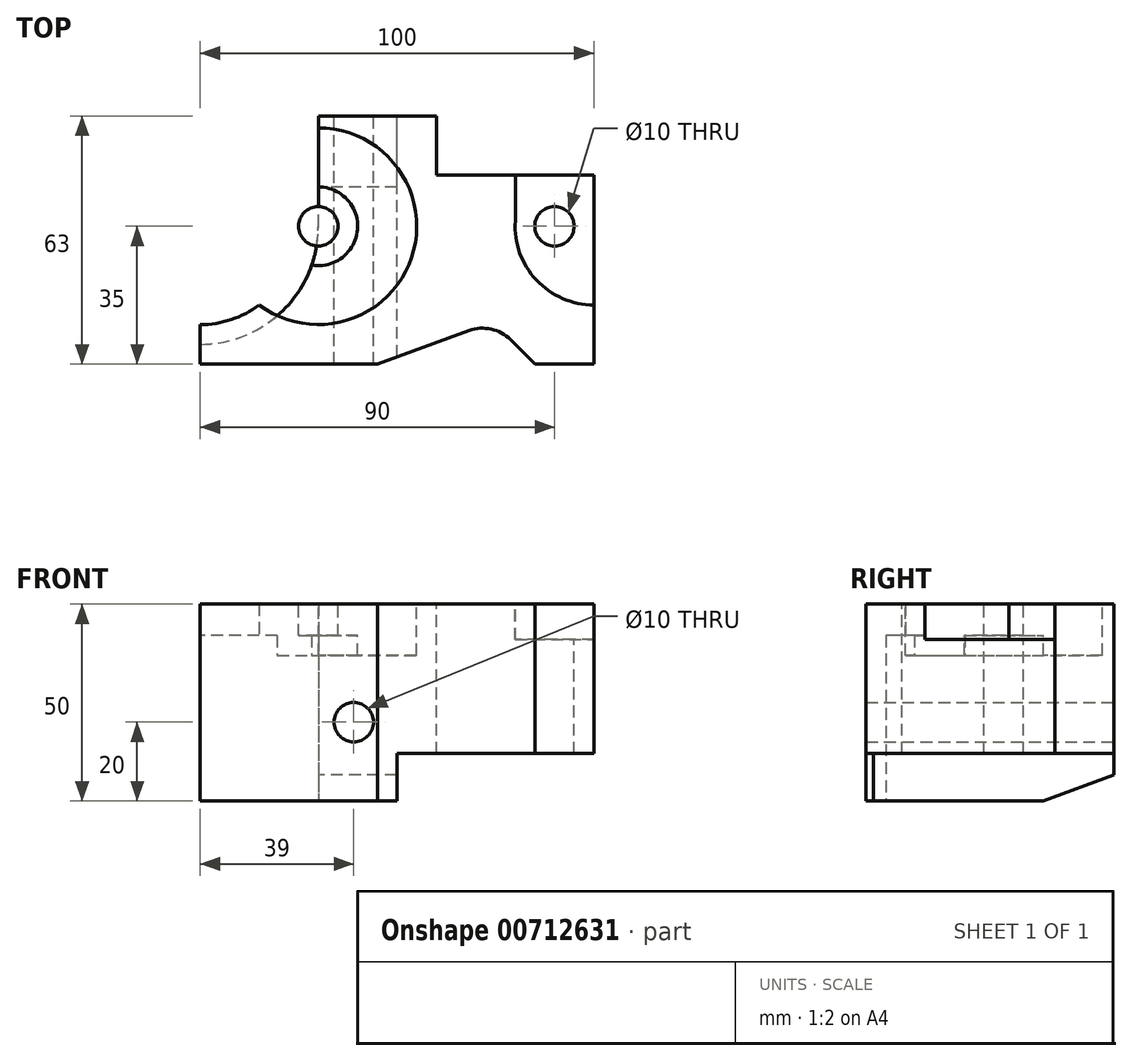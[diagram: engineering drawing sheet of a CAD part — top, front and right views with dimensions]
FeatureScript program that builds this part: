
annotation { "Feature Type Name" : "Feature", "Feature Type Description" : "" }
export const myFeature = defineFeature(function(context is Context, id is Id, definition is map)
    precondition{}
    {
        {
            var Q0;
            Q0=qCreatedBy(makeId("Top.planeOp"),FACE);
            var sketch = newSketch(context, id + "F0", { "sketchPlane" : qUnion([Q0])});
            skLineSegment(sketch, "E0.bottom", {"start": v(0, 0) * mm, "end": v(-100, 0) * mm});
            skLineSegment(sketch, "E0.top", {"start": v(0, 63) * mm, "end": v(-100, 63) * mm});
            skLineSegment(sketch, "E0.left", {"start": v(0, 0) * mm, "end": v(0, 63) * mm});
            skLineSegment(sketch, "E0.right", {"start": v(-100, 0) * mm, "end": v(-100, 63) * mm});
            skSolve(sketch);
        }
        {
            var Q0;
            Q0=makeQuery(id+"F0.imprint","IMPRINT",FACE,{"disambiguationData":[TD([[makeQuery(id+"F0.imprint","IMPRINT",EDGE,{"derivedFrom":sQuery(id+"F0.wireOp",EDGE,"E0.bottom")}),-1.0]])]});
            extrude(context, id + "F1", {"entities" : qUnion([Q0]), "depth" : 50 * mm, "offsetDistance" : 25 * mm});
        }
        {
            var Q0;
            Q0=makeQuery(id+"F1.opExtrude","CAP_FACE",FACE,{"disambiguationData":[OSD([sQuery(id+"F0.wireOp",EDGE,"E0.bottom"),sQuery(id+"F0.wireOp",EDGE,"E0.top"),sQuery(id+"F0.wireOp",EDGE,"E0.left"),sQuery(id+"F0.wireOp",EDGE,"E0.right")])],"isStart":false});
            var sketch = newSketch(context, id + "F2", { "sketchPlane" : qUnion([Q0])});
            skLineSegment(sketch, "E1.bottom", {"start": v(0, 63) * mm, "end": v(-40, 63) * mm});
            skLineSegment(sketch, "E1.top", {"start": v(0, 48) * mm, "end": v(-40, 48) * mm});
            skLineSegment(sketch, "E1.left", {"start": v(0, 63) * mm, "end": v(0, 48) * mm});
            skLineSegment(sketch, "E1.right", {"start": v(-40, 63) * mm, "end": v(-40, 48) * mm});
            skSolve(sketch);
        }
        {
            var Q0;
            Q0=makeQuery(id+"F2.imprint","IMPRINT",FACE,{"disambiguationData":[TD([[makeQuery(id+"F2.imprint","IMPRINT",EDGE,{"derivedFrom":sQuery(id+"F2.wireOp",EDGE,"E1.bottom")}),1.0]])]});
            extrude(context, id + "F3", {"entities" : qUnion([Q0]), "operationType" : NewBodyOperationType.REMOVE, "endBound" : BoundingType.THROUGH_ALL, "oppositeDirection" : true, "depth" : 25 * mm, "offsetDistance" : 25 * mm});
        }
        {
            var Q0;
            Q0=makeQuery(id+"F1.opExtrude","CAP_FACE",FACE,{"disambiguationData":[OSD([sQuery(id+"F0.wireOp",EDGE,"E0.bottom"),sQuery(id+"F0.wireOp",EDGE,"E0.top"),sQuery(id+"F0.wireOp",EDGE,"E0.left"),sQuery(id+"F0.wireOp",EDGE,"E0.right")])],"isStart":false});
            var sketch = newSketch(context, id + "F4", { "sketchPlane" : qUnion([Q0])});
            skArc(sketch, "E2", {"start": v(-19.96, 36.28) * mm, "mid": v(-14.59, 21.32) * mm, "end": v(0, 15) * mm});
            skLineSegment(sketch, "E3", {"start": v(-19.96, 33.72) * mm, "end": v(-19.96, 48) * mm});
            skLineSegment(sketch, "E4", {"start": v(-19.96, 48) * mm, "end": v(0, 48) * mm});
            skLineSegment(sketch, "E5", {"start": v(0, 48) * mm, "end": v(0, 15) * mm});
            skSolve(sketch);
        }
        {
            var Q0;
            Q0 = qSketchRegion(id + "F4", true);
            extrude(context, id + "F5", {"entities" : qUnion([Q0]), "operationType" : NewBodyOperationType.REMOVE, "oppositeDirection" : true, "depth" : 9 * mm, "offsetDistance" : 25 * mm});
        }
        {
            var Q0;
            Q0=makeQuery(id+"F5.boolean.opBoolean","COPY",FACE,{"derivedFrom":makeQuery(id+"F5.opExtrude","CAP_FACE",FACE,{"disambiguationData":[OSD([sQuery(id+"F4.wireOp",EDGE,"E2"),sQuery(id+"F4.wireOp",EDGE,"E3"),sQuery(id+"F4.wireOp",EDGE,"E4"),sQuery(id+"F4.wireOp",EDGE,"E5")])],"isStart":false})});
            var sketch = newSketch(context, id + "F6", { "sketchPlane" : qUnion([Q0])});
            skCircle(sketch, "E6", {"center": v(-10, 35) * mm, "radius": 5 * mm});
            skSolve(sketch);
        }
        {
            var Q0;
            Q0 = qSketchRegion(id + "F6", true);
            extrude(context, id + "F7", {"entities" : qUnion([Q0]), "operationType" : NewBodyOperationType.REMOVE, "endBound" : BoundingType.THROUGH_ALL, "oppositeDirection" : true, "depth" : 25 * mm, "offsetDistance" : 25 * mm});
        }
        {
            var Q0;
            Q0=makeQuery(id+"F1.opExtrude","SWEPT_FACE",FACE,{"disambiguationData":[OSD([sQuery(id+"F0.wireOp",EDGE,"E0.top")])]});
            var sketch = newSketch(context, id + "F8", { "sketchPlane" : qUnion([Q0])});
            skLineSegment(sketch, "E7.bottom", {"start": v(50, 0) * mm, "end": v(0, 0) * mm});
            skLineSegment(sketch, "E7.top", {"start": v(50, 12) * mm, "end": v(0, 12) * mm});
            skLineSegment(sketch, "E7.left", {"start": v(50, 0) * mm, "end": v(50, 12) * mm});
            skLineSegment(sketch, "E7.right", {"start": v(0, 0) * mm, "end": v(0, 12) * mm});
            skSolve(sketch);
        }
        {
            var Q0;
            Q0 = qSketchRegion(id + "F8", true);
            extrude(context, id + "F9", {"entities" : qUnion([Q0]), "operationType" : NewBodyOperationType.REMOVE, "endBound" : BoundingType.THROUGH_ALL, "oppositeDirection" : true, "depth" : 25 * mm, "offsetDistance" : 25 * mm});
        }
        {
            var Q0;
            Q0=makeQuery(id+"F1.opExtrude","CAP_FACE",FACE,{"disambiguationData":[OSD([sQuery(id+"F0.wireOp",EDGE,"E0.bottom"),sQuery(id+"F0.wireOp",EDGE,"E0.top"),sQuery(id+"F0.wireOp",EDGE,"E0.left"),sQuery(id+"F0.wireOp",EDGE,"E0.right")])],"isStart":false});
            var sketch = newSketch(context, id + "F10", { "sketchPlane" : qUnion([Q0])});
            skLineSegment(sketch, "E8", {"start": v(-15, 0) * mm, "end": v(-21.17, 6.17) * mm});
            skLineSegment(sketch, "E9", {"start": v(-31.66, 8.5) * mm, "end": v(-55, 0) * mm});
            skPoint(sketch, "E10.visualSharp", {"position": v(-25.67, 10.67) * mm});
            skArc(sketch, "E10.filletArc", {"start": v(-21.17, 6.17) * mm, "mid": v(-26.08, 8.86) * mm, "end": v(-31.66, 8.5) * mm});
            skLineSegment(sketch, "E11", {"start": v(-55, 0) * mm, "end": v(-15, 0) * mm});
            skSolve(sketch);
        }
        {
            var Q0;
            Q0 = qSketchRegion(id + "F10", true);
            extrude(context, id + "F11", {"entities" : qUnion([Q0]), "operationType" : NewBodyOperationType.REMOVE, "endBound" : BoundingType.THROUGH_ALL, "oppositeDirection" : true, "depth" : 25 * mm, "offsetDistance" : 25 * mm});
        }
        {
            var Q0;
            Q0=makeQuery(id+"F1.opExtrude","CAP_FACE",FACE,{"disambiguationData":[OSD([sQuery(id+"F0.wireOp",EDGE,"E0.bottom"),sQuery(id+"F0.wireOp",EDGE,"E0.top"),sQuery(id+"F0.wireOp",EDGE,"E0.left"),sQuery(id+"F0.wireOp",EDGE,"E0.right")])],"isStart":false});
            var sketch = newSketch(context, id + "F12", { "sketchPlane" : qUnion([Q0])});
            skCircle(sketch, "E12", {"center": v(-70, 35) * mm, "radius": 5 * mm});
            skCircle(sketch, "E13", {"center": v(-70, 35) * mm, "radius": 10 * mm});
            skCircle(sketch, "E14", {"center": v(-70, 35) * mm, "radius": 25 * mm});
            skSolve(sketch);
        }
        {
            var Q0;
            Q0=makeQuery(id+"F12.imprint","IMPRINT",FACE,{"disambiguationData":[TD([[makeQuery(id+"F12.imprint","IMPRINT",EDGE,{"derivedFrom":sQuery(id+"F12.wireOp",EDGE,"E12")}),-1.0]])]});
            extrude(context, id + "F13", {"entities" : qUnion([Q0]), "operationType" : NewBodyOperationType.REMOVE, "oppositeDirection" : true, "depth" : 8 * mm, "offsetDistance" : 25 * mm});
        }
        {
            var Q0;
            Q0 = qSketchRegion(id + "F12", true);
            extrude(context, id + "F14", {"entities" : qUnion([Q0]), "operationType" : NewBodyOperationType.ADD, "oppositeDirection" : true, "depth" : 13 * mm, "offsetDistance" : 25 * mm});
        }
        {
            var Q0;
            {var subQ0=sQuery(id+"F0.wireOp",EDGE,"E0.right");var subQ1=sQuery(id+"F0.wireOp",EDGE,"E0.top");var subQ2=sQuery(id+"F0.wireOp",EDGE,"E0.bottom");var subQ3=sQuery(id+"F0.wireOp",EDGE,"E0.left");Q0=makeQuery(id+"F13.boolean.opBoolean","SPLIT",FACE,{"disambiguationData":[TD([makeQuery(id+"F1.opExtrude","SWEPT_FACE",FACE,{"disambiguationData":[OSD([subQ2])]})])],"derivedFrom":makeQuery(id+"F1.opExtrude","CAP_FACE",FACE,{"disambiguationData":[OSD([subQ2,subQ1,subQ3,subQ0])],"isStart":false})});}
            var sketch = newSketch(context, id + "F15", { "sketchPlane" : qUnion([Q0])});
            skCircle(sketch, "E15", {"center": v(-70, 35) * mm, "radius": 25 * mm});
            skSolve(sketch);
        }
        {
            var Q0;
            Q0=makeQuery(id+"F15.imprint","IMPRINT",FACE,{"disambiguationData":[TD([[makeQuery(id+"F15.imprint","IMPRINT",EDGE,{"derivedFrom":sQuery(id+"F15.wireOp",EDGE,"E15")}),1.0]])]});
            extrude(context, id + "F16", {"entities" : qUnion([Q0]), "operationType" : NewBodyOperationType.REMOVE, "oppositeDirection" : true, "depth" : 13 * mm, "offsetDistance" : 25 * mm});
        }
        {
            var Q0;
            Q0=makeQuery(id+"F1.opExtrude","SWEPT_FACE",FACE,{"disambiguationData":[OSD([sQuery(id+"F0.wireOp",EDGE,"E0.right")])]});
            var sketch = newSketch(context, id + "F17", { "sketchPlane" : qUnion([Q0])});
            skLineSegment(sketch, "E16", {"start": v(-63, 0) * mm, "end": v(-45, 0) * mm});
            skLineSegment(sketch, "E17", {"start": v(-45, 0) * mm, "end": v(-63, 6.55) * mm});
            skLineSegment(sketch, "E18", {"start": v(-63, 6.55) * mm, "end": v(-63, 0) * mm});
            skSolve(sketch);
        }
        {
            var Q0;
            Q0=makeQuery(id+"F17.imprint","IMPRINT",FACE,{"disambiguationData":[TD([[makeQuery(id+"F17.imprint","IMPRINT",EDGE,{"derivedFrom":sQuery(id+"F17.wireOp",EDGE,"E16")}),-1.0]])]});
            extrude(context, id + "F18", {"entities" : qUnion([Q0]), "operationType" : NewBodyOperationType.REMOVE, "endBound" : BoundingType.THROUGH_ALL, "oppositeDirection" : true, "depth" : 25 * mm, "offsetDistance" : 25 * mm});
        }
        {
            var Q0;
            Q0=makeQuery(id+"F1.opExtrude","CAP_FACE",FACE,{"disambiguationData":[OSD([sQuery(id+"F0.wireOp",EDGE,"E0.bottom"),sQuery(id+"F0.wireOp",EDGE,"E0.top"),sQuery(id+"F0.wireOp",EDGE,"E0.left"),sQuery(id+"F0.wireOp",EDGE,"E0.right")])],"isStart":true});
            var sketch = newSketch(context, id + "F19", { "sketchPlane" : qUnion([Q0])});
            skCircle(sketch, "E19", {"center": v(-100, -35) * mm, "radius": 25 * mm});
            skCircle(sketch, "E20", {"center": v(-100, -35) * mm, "radius": 30 * mm});
            skLineSegment(sketch, "E21", {"start": v(-70, -35) * mm, "end": v(-70, -63) * mm});
            skLineSegment(sketch, "E22", {"start": v(-70, -63) * mm, "end": v(-99.79, -63) * mm});
            skSolve(sketch);
        }
        {
            var Q0;
            {var subQ0=sQuery(id+"F19.wireOp",EDGE,"E19");var subQ1=sQuery(id+"F0.wireOp",EDGE,"E0.right");var subQ2=makeQuery(id+"F1.opExtrude","CAP_EDGE",EDGE,{"disambiguationData":[OSD([subQ1])],"isStart":true});var subQ3=makeQuery(id+"F19.imprint","INTERSECT",VERTEX,{"derivedFrom":[subQ2,subQ0]});Q0=makeQuery(id+"F19.imprint","IMPRINT",FACE,{"disambiguationData":[TD([[makeQuery(id+"F19.imprint","IMPRINT",EDGE,{"disambiguationData":[TD([[subQ3,1.0]])],"derivedFrom":subQ0}),1.0]])]});}
            var Q1;
            {var subQ0=sQuery(id+"F19.wireOp",EDGE,"E19");var subQ1=sQuery(id+"F0.wireOp",EDGE,"E0.right");var subQ2=makeQuery(id+"F1.opExtrude","CAP_EDGE",EDGE,{"disambiguationData":[OSD([subQ1])],"isStart":true});var subQ3=makeQuery(id+"F19.imprint","INTERSECT",VERTEX,{"derivedFrom":[subQ2,subQ0]});Q1=makeQuery(id+"F19.imprint","IMPRINT",FACE,{"disambiguationData":[TD([[makeQuery(id+"F19.imprint","IMPRINT",EDGE,{"disambiguationData":[TD([[subQ3,-1.0]])],"derivedFrom":subQ0}),1.0]])]});}
            extrude(context, id + "F20", {"entities" : qUnion([Q0, Q1]), "operationType" : NewBodyOperationType.REMOVE, "endBound" : BoundingType.THROUGH_ALL, "oppositeDirection" : true, "depth" : 25 * mm, "offsetDistance" : 25 * mm});
        }
        {
            var Q0;
            Q0 = qSketchRegion(id + "F19", true);
            extrude(context, id + "F21", {"entities" : qUnion([Q0]), "operationType" : NewBodyOperationType.REMOVE, "oppositeDirection" : true, "depth" : 42 * mm, "offsetDistance" : 25 * mm});
        }
        {
            var Q0;
            {var subQ0=sQuery(id+"F19.wireOp",EDGE,"E19");var subQ1=sQuery(id+"F19.wireOp",EDGE,"E21");Q0=makeQuery(id+"F21.boolean.opBoolean","COPY",FACE,{"disambiguationData":[TD([makeQuery(id+"F1.opExtrude","SWEPT_FACE",FACE,{"disambiguationData":[OSD([sQuery(id+"F0.wireOp",EDGE,"E0.top")])]}),makeQuery(id+"F1.opExtrude","SWEPT_FACE",FACE,{"disambiguationData":[OSD([sQuery(id+"F0.wireOp",EDGE,"E0.right")])]}),makeQuery(id+"F16.boolean.opBoolean","COPY",FACE,{"derivedFrom":makeQuery(id+"F16.opExtrude","SWEPT_FACE",FACE,{"disambiguationData":[OSD([sQuery(id+"F15.wireOp",EDGE,"E15")])]})}),makeQuery(id+"F20.boolean.opBoolean","COPY",FACE,{"derivedFrom":makeQuery(id+"F20.opExtrude","SWEPT_FACE",FACE,{"disambiguationData":[OSD([subQ0])]})}),makeQuery(id+"F21.opExtrude","SWEPT_FACE",FACE,{"disambiguationData":[OSD([subQ1])]})])],"derivedFrom":makeQuery(id+"F21.opExtrude","CAP_FACE",FACE,{"disambiguationData":[OSD([subQ0,sQuery(id+"F19.wireOp",EDGE,"E20"),subQ1,sQuery(id+"F19.wireOp",EDGE,"E22")])],"isStart":false})});}
            var sketch = newSketch(context, id + "F22", { "sketchPlane" : qUnion([Q0])});
            skLineSegment(sketch, "E23.bottom", {"start": v(-70, -63) * mm, "end": v(-100.84, -63) * mm});
            skLineSegment(sketch, "E23.top", {"start": v(-70, -50.54) * mm, "end": v(-100.84, -50.54) * mm});
            skLineSegment(sketch, "E23.left", {"start": v(-70, -63) * mm, "end": v(-70, -50.54) * mm});
            skLineSegment(sketch, "E23.right", {"start": v(-100.84, -63) * mm, "end": v(-100.84, -50.54) * mm});
            skSolve(sketch);
        }
        {
            var Q0;
            {var subQ5=sQuery(id+"F22.wireOp",EDGE,"E23.top");Q0=makeQuery(id+"F22.imprint","IMPRINT",FACE,{"disambiguationData":[TD([[makeQuery(id+"F22.imprint","IMPRINT",EDGE,{"derivedFrom":subQ5}),1.0]])]});}
            var Q1;
            {var subQ0=sQuery(id+"F19.wireOp",EDGE,"E19");Q1=makeQuery(id+"F22.imprint","IMPRINT",FACE,{"disambiguationData":[TD([[makeQuery(id+"F22.imprint","IMPRINT",EDGE,{"derivedFrom":makeQuery(id+"F21.boolean.opBoolean","COPY",EDGE,{"disambiguationData":[OD(1.0)],"derivedFrom":makeQuery(id+"F21.opExtrude","CAP_EDGE",EDGE,{"disambiguationData":[OSD([subQ0])],"isStart":false})})}),-1.0]])]});}
            extrude(context, id + "F23", {"entities" : qUnion([Q0, Q1]), "operationType" : NewBodyOperationType.REMOVE, "endBound" : BoundingType.THROUGH_ALL, "oppositeDirection" : true, "depth" : 25 * mm, "offsetDistance" : 25 * mm});
        }
        {
            var Q0;
            Q0=makeQuery(id+"F1.opExtrude","SWEPT_FACE",FACE,{"disambiguationData":[OSD([sQuery(id+"F0.wireOp",EDGE,"E0.top")])]});
            var sketch = newSketch(context, id + "F24", { "sketchPlane" : qUnion([Q0])});
            skCircle(sketch, "E24", {"center": v(61, 20) * mm, "radius": 5 * mm});
            skSolve(sketch);
        }
        {
            var Q0;
            Q0=makeQuery(id+"F24.imprint","IMPRINT",FACE,{"disambiguationData":[TD([[makeQuery(id+"F24.imprint","IMPRINT",EDGE,{"derivedFrom":sQuery(id+"F24.wireOp",EDGE,"E24")}),1.0]])]});
            extrude(context, id + "F25", {"entities" : qUnion([Q0]), "operationType" : NewBodyOperationType.REMOVE, "endBound" : BoundingType.THROUGH_ALL, "oppositeDirection" : true, "depth" : 25 * mm, "offsetDistance" : 25 * mm});
        }
    });
